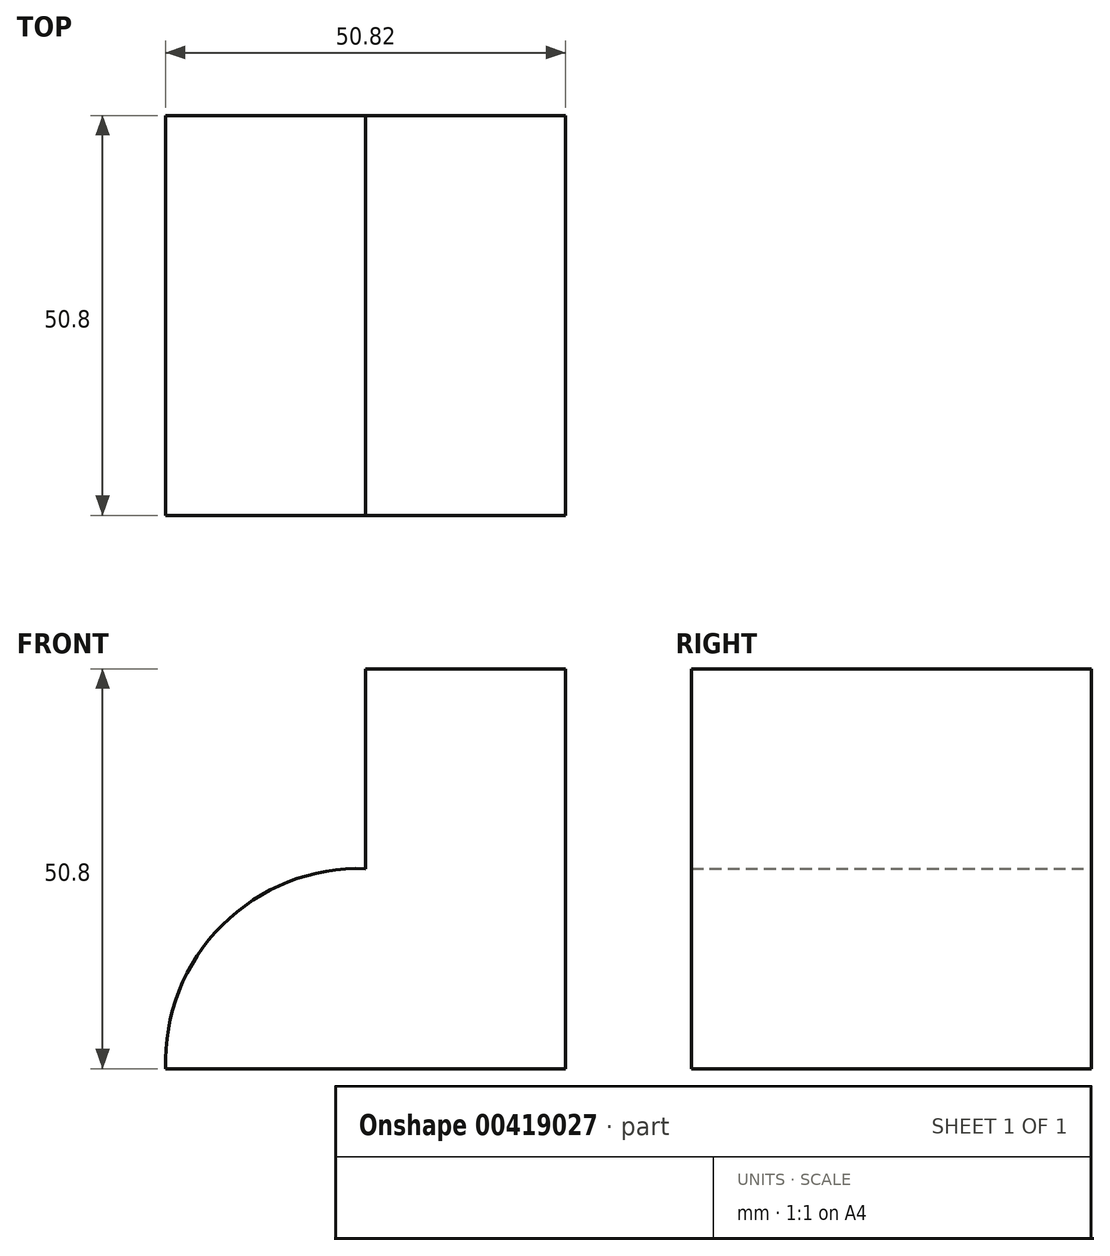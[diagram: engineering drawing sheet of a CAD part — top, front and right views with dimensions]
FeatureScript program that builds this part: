
annotation { "Feature Type Name" : "Feature", "Feature Type Description" : "" }
export const myFeature = defineFeature(function(context is Context, id is Id, definition is map)
    precondition{}
    {
        {
            var Q0;
            Q0=qCreatedBy(makeId("Front.planeOp"),FACE);
            var sketch = newSketch(context, id + "F0", { "sketchPlane" : qUnion([Q0])});
            skLineSegment(sketch, "E0", {"start": v(0, 0) * mm, "end": v(0, 50.8) * mm});
            skLineSegment(sketch, "E1", {"start": v(0, 50.8) * mm, "end": v(-25.4, 50.8) * mm});
            skLineSegment(sketch, "E2", {"start": v(-25.4, 50.8) * mm, "end": v(-25.4, 25.4) * mm});
            skLineSegment(sketch, "E3", {"start": v(-25.4, 0) * mm, "end": v(0, 0) * mm});
            skLineSegment(sketch, "E4", {"start": v(-25.4, 0) * mm, "end": v(-50.8, 0) * mm});
            skPoint(sketch, "E5.end.orphan", {"position": v(-45.83, 0) * mm});
            skPoint(sketch, "E5.start.orphan", {"position": v(-25.4, 25.4) * mm});
            skArc(sketch, "E6", {"start": v(-25.4, 25.4) * mm, "mid": v(-43.63, 18.23) * mm, "end": v(-50.8, 0) * mm});
            skSolve(sketch);
        }
        {
            var Q0;
            Q0 = qSketchRegion(id + "F0", true);
            var Q1;
            Q1=makeQuery(id+"F0.imprint","IMPRINT",FACE,{"disambiguationData":[TD([[makeQuery(id+"F0.imprint","IMPRINT",EDGE,{"derivedFrom":sQuery(id+"F0.wireOp",EDGE,"E0")}),1.0]])]});
            extrude(context, id + "F1", {"entities" : qUnion([Q0, Q1]), "depth" : 50.8 * mm});
        }
    });
